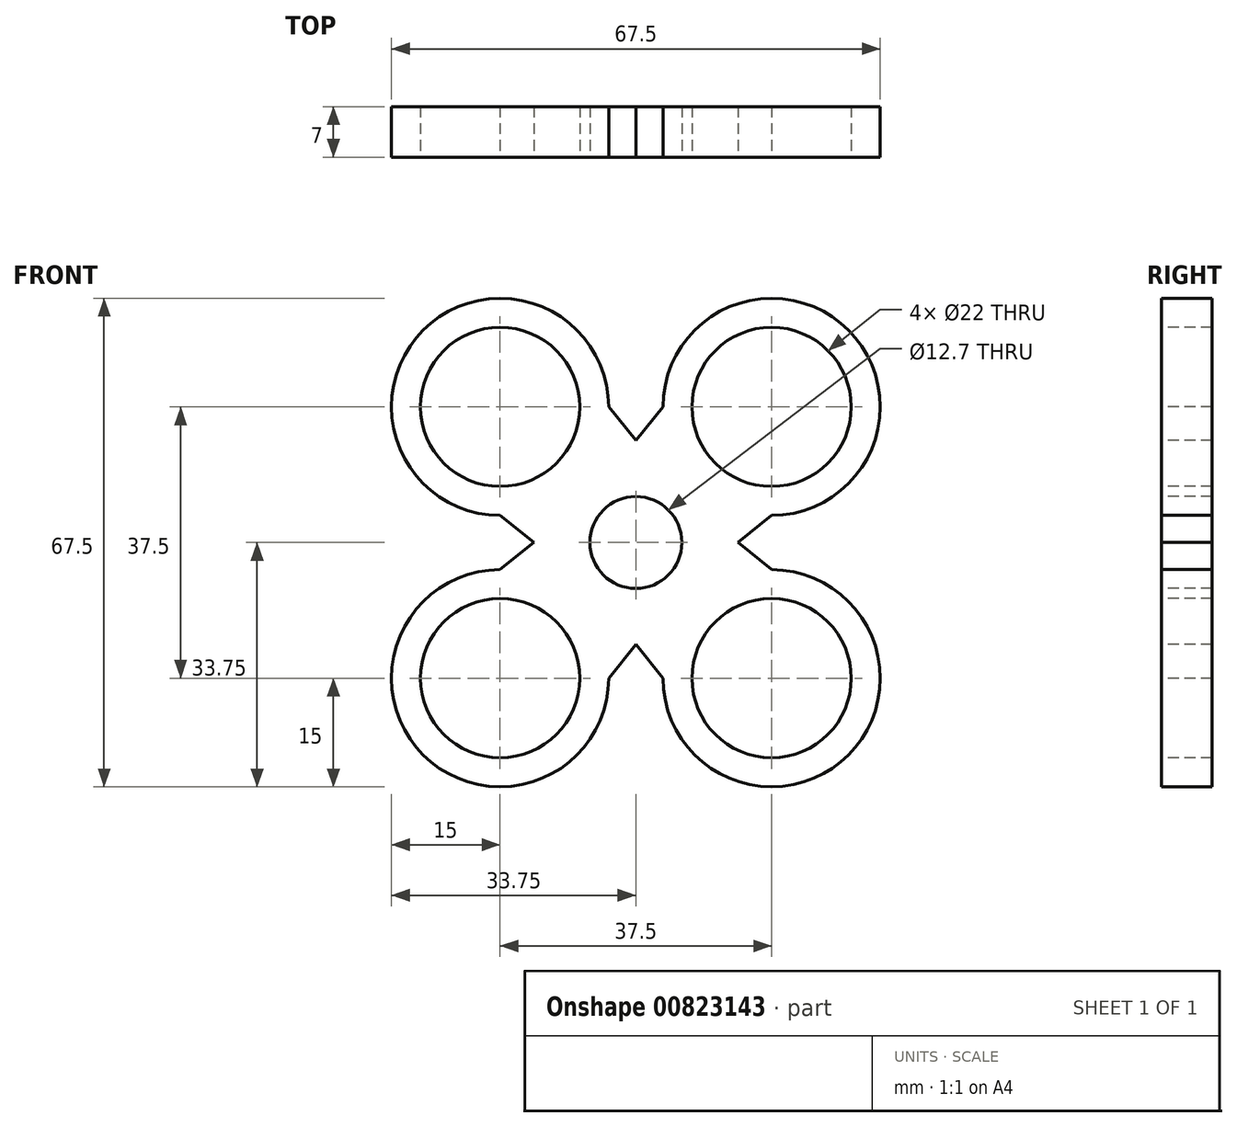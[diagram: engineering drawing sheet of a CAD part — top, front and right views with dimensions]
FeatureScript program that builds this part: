
annotation { "Feature Type Name" : "Feature", "Feature Type Description" : "" }
export const myFeature = defineFeature(function(context is Context, id is Id, definition is map)
    precondition{}
    {
        {
            var Q0;
            Q0=qCreatedBy(makeId("Front.planeOp"),FACE);
            var sketch = newSketch(context, id + "F0", { "sketchPlane" : qUnion([Q0])});
            skCircle(sketch, "E0", {"center": v(0, 0) * mm, "radius": 37.5 * mm});
            skSolve(sketch);
        }
        {
            var Q0;
            Q0=makeQuery(id+"F0.imprint","IMPRINT",FACE,{"disambiguationData":[TD([[makeQuery(id+"F0.imprint","IMPRINT",EDGE,{"derivedFrom":sQuery(id+"F0.wireOp",EDGE,"E0")}),1.0]])]});
            extrude(context, id + "F1", {"entities" : qUnion([Q0]), "depth" : 7 * mm, "offsetDistance" : 25 * mm});
        }
        {
            var Q0;
            Q0=makeQuery(id+"F1.opExtrude","CAP_FACE",FACE,{"disambiguationData":[OSD([sQuery(id+"F0.wireOp",EDGE,"E0")])],"isStart":false});
            var sketch = newSketch(context, id + "F2", { "sketchPlane" : qUnion([Q0])});
            skCircle(sketch, "E1", {"center": v(0, 0) * mm, "radius": 6.35 * mm});
            skSolve(sketch);
        }
        {
            var Q0;
            Q0=makeQuery(id+"F2.imprint","IMPRINT",FACE,{"disambiguationData":[TD([[makeQuery(id+"F2.imprint","IMPRINT",EDGE,{"derivedFrom":sQuery(id+"F2.wireOp",EDGE,"E1")}),1.0]])]});
            extrude(context, id + "F3", {"entities" : qUnion([Q0]), "operationType" : NewBodyOperationType.REMOVE, "endBound" : BoundingType.THROUGH_ALL, "oppositeDirection" : true, "depth" : 25 * mm, "offsetDistance" : 25 * mm});
        }
        {
            var Q0;
            Q0=makeQuery(id+"F1.opExtrude","CAP_FACE",FACE,{"disambiguationData":[OSD([sQuery(id+"F0.wireOp",EDGE,"E0")])],"isStart":false});
            var sketch = newSketch(context, id + "F4", { "sketchPlane" : qUnion([Q0])});
            skLineSegment(sketch, "E2", {"start": v(0, 37.5) * mm, "end": v(37.5, 0) * mm});
            skLineSegment(sketch, "E3", {"start": v(37.5, 0) * mm, "end": v(0, -37.5) * mm});
            skLineSegment(sketch, "E4", {"start": v(0, -37.5) * mm, "end": v(-37.5, 0) * mm});
            skLineSegment(sketch, "E5", {"start": v(-37.5, 0) * mm, "end": v(0, 37.5) * mm});
            skLineSegment(sketch, "E6", {"start": v(0, 37.5) * mm, "end": v(0, -37.5) * mm});
            skLineSegment(sketch, "E7", {"start": v(-37.5, 0) * mm, "end": v(37.5, 0) * mm});
            skLineSegment(sketch, "E8", {"start": v(-18.75, 18.75) * mm, "end": v(18.75, -18.75) * mm});
            skLineSegment(sketch, "E9", {"start": v(18.75, -18.75) * mm, "end": v(18.75, 18.75) * mm});
            skLineSegment(sketch, "E10", {"start": v(18.75, 18.75) * mm, "end": v(-18.75, 18.75) * mm});
            skLineSegment(sketch, "E11", {"start": v(-18.75, 18.75) * mm, "end": v(-18.75, -18.75) * mm});
            skLineSegment(sketch, "E12", {"start": v(-18.75, -18.75) * mm, "end": v(18.75, -18.75) * mm});
            skLineSegment(sketch, "E13", {"start": v(-18.75, -18.75) * mm, "end": v(18.75, 18.75) * mm});
            skCircle(sketch, "E14", {"center": v(-18.75, 18.75) * mm, "radius": 15 * mm});
            skCircle(sketch, "E15", {"center": v(-18.75, -18.75) * mm, "radius": 15 * mm});
            skCircle(sketch, "E16", {"center": v(18.75, 18.75) * mm, "radius": 15 * mm});
            skCircle(sketch, "E17", {"center": v(18.75, -18.75) * mm, "radius": 15 * mm});
            skLineSegment(sketch, "E18", {"start": v(3.75, -18.75) * mm, "end": v(0, -6.35) * mm});
            skLineSegment(sketch, "E19", {"start": v(0, -6.35) * mm, "end": v(-3.75, -18.75) * mm});
            skLineSegment(sketch, "E20", {"start": v(-3.75, -18.75) * mm, "end": v(3.75, -18.75) * mm});
            skLineSegment(sketch, "E21", {"start": v(18.75, -3.75) * mm, "end": v(6.35, 0) * mm});
            skLineSegment(sketch, "E22", {"start": v(18.75, 3.75) * mm, "end": v(6.35, 0) * mm});
            skLineSegment(sketch, "E23", {"start": v(18.75, 3.75) * mm, "end": v(18.75, -3.75) * mm});
            skLineSegment(sketch, "E24", {"start": v(-3.75, 18.75) * mm, "end": v(0, 6.35) * mm});
            skLineSegment(sketch, "E25", {"start": v(0, 6.35) * mm, "end": v(3.75, 18.75) * mm});
            skLineSegment(sketch, "E26", {"start": v(3.75, 18.75) * mm, "end": v(-3.75, 18.75) * mm});
            skLineSegment(sketch, "E27", {"start": v(-18.75, 3.75) * mm, "end": v(-6.35, 0) * mm});
            skLineSegment(sketch, "E28", {"start": v(-6.35, 0) * mm, "end": v(-18.75, -3.75) * mm});
            skLineSegment(sketch, "E29", {"start": v(-18.75, -3.75) * mm, "end": v(-18.75, 3.75) * mm});
            skLineSegment(sketch, "E30", {"start": v(18.75, -3.75) * mm, "end": v(-3.75, 18.75) * mm});
            skLineSegment(sketch, "E31", {"start": v(-18.75, 3.75) * mm, "end": v(3.75, -18.75) * mm});
            skLineSegment(sketch, "E32", {"start": v(-3.75, -18.75) * mm, "end": v(18.75, 3.75) * mm});
            skLineSegment(sketch, "E33", {"start": v(-18.75, -3.75) * mm, "end": v(3.75, 18.75) * mm});
            skLineSegment(sketch, "E34", {"start": v(-3.75, 18.75) * mm, "end": v(13, -2) * mm});
            skLineSegment(sketch, "E35", {"start": v(13, -2) * mm, "end": v(3.75, 18.75) * mm});
            skLineSegment(sketch, "E36", {"start": v(3.75, 18.75) * mm, "end": v(-13, -2) * mm});
            skLineSegment(sketch, "E37", {"start": v(-13, -2) * mm, "end": v(-3.75, 18.75) * mm});
            skLineSegment(sketch, "E38", {"start": v(-18.75, 3.75) * mm, "end": v(2, 13) * mm});
            skLineSegment(sketch, "E39", {"start": v(2, 13) * mm, "end": v(-18.75, -3.75) * mm});
            skLineSegment(sketch, "E40", {"start": v(-18.75, 3.75) * mm, "end": v(2, -13) * mm});
            skLineSegment(sketch, "E41", {"start": v(2, -13) * mm, "end": v(-18.75, -3.75) * mm});
            skLineSegment(sketch, "E42", {"start": v(-3.75, -18.75) * mm, "end": v(-13, 2) * mm});
            skLineSegment(sketch, "E43", {"start": v(-13, 2) * mm, "end": v(3.75, -18.75) * mm});
            skLineSegment(sketch, "E44", {"start": v(3.75, -18.75) * mm, "end": v(13, 2) * mm});
            skLineSegment(sketch, "E45", {"start": v(13, 2) * mm, "end": v(-3.75, -18.75) * mm});
            skLineSegment(sketch, "E46", {"start": v(18.75, 3.75) * mm, "end": v(-2, 13) * mm});
            skLineSegment(sketch, "E47", {"start": v(-2, 13) * mm, "end": v(18.75, -3.75) * mm});
            skLineSegment(sketch, "E48", {"start": v(18.75, 3.75) * mm, "end": v(-2, -13) * mm});
            skLineSegment(sketch, "E49", {"start": v(-2, -13) * mm, "end": v(18.75, -3.75) * mm});
            skSolve(sketch);
        }
        {
            var Q0;
            {var subQ0=sQuery(id+"F4.wireOp",EDGE,"E5");var subQ3=sQuery(id+"F4.wireOp",EDGE,"E14");var subQ4=makeQuery(id+"F4.imprint","INTERSECT",VERTEX,{"disambiguationData":[OD(1.0)],"derivedFrom":[subQ0,subQ3]});Q0=makeQuery(id+"F4.imprint","IMPRINT",FACE,{"disambiguationData":[TD([[makeQuery(id+"F4.imprint","IMPRINT",EDGE,{"disambiguationData":[TD([[subQ4,-1.0]])],"derivedFrom":subQ3}),-1.0]])]});}
            var Q1;
            {var subQ0=sQuery(id+"F4.wireOp",EDGE,"E2");var subQ3=sQuery(id+"F4.wireOp",EDGE,"E16");var subQ4=makeQuery(id+"F4.imprint","INTERSECT",VERTEX,{"disambiguationData":[OD(0.0)],"derivedFrom":[subQ0,subQ3]});Q1=makeQuery(id+"F4.imprint","IMPRINT",FACE,{"disambiguationData":[TD([[makeQuery(id+"F4.imprint","IMPRINT",EDGE,{"disambiguationData":[TD([[subQ4,1.0]])],"derivedFrom":subQ3}),-1.0]])]});}
            var Q2;
            {var subQ1=sQuery(id+"F4.wireOp",EDGE,"E5");var subQ3=sQuery(id+"F4.wireOp",EDGE,"E14");var subQ4=makeQuery(id+"F4.imprint","INTERSECT",VERTEX,{"disambiguationData":[OD(1.0)],"derivedFrom":[subQ1,subQ3]});Q2=makeQuery(id+"F4.imprint","IMPRINT",FACE,{"disambiguationData":[TD([[makeQuery(id+"F4.imprint","IMPRINT",EDGE,{"disambiguationData":[TD([[subQ4,-1.0]])],"derivedFrom":subQ1}),-1.0]])]});}
            var Q3;
            {var subQ1=sQuery(id+"F4.wireOp",EDGE,"E2");var subQ3=sQuery(id+"F4.wireOp",EDGE,"E16");var subQ4=makeQuery(id+"F4.imprint","INTERSECT",VERTEX,{"disambiguationData":[OD(0.0)],"derivedFrom":[subQ1,subQ3]});Q3=makeQuery(id+"F4.imprint","IMPRINT",FACE,{"disambiguationData":[TD([[makeQuery(id+"F4.imprint","IMPRINT",EDGE,{"disambiguationData":[TD([[subQ4,1.0]])],"derivedFrom":subQ1}),-1.0]])]});}
            var Q4;
            {var subQ0=sQuery(id+"F4.wireOp",EDGE,"E26");var subQ1=sQuery(id+"F4.wireOp",EDGE,"E6");var subQ2=makeQuery(id+"F4.imprint","INTERSECT",VERTEX,{"derivedFrom":[subQ1,subQ0]});Q4=makeQuery(id+"F4.imprint","IMPRINT",FACE,{"disambiguationData":[TD([[makeQuery(id+"F4.imprint","IMPRINT",EDGE,{"disambiguationData":[TD([[subQ2,-1.0]])],"derivedFrom":subQ1}),-1.0]])]});}
            var Q5;
            {var subQ0=sQuery(id+"F4.wireOp",EDGE,"E34");var subQ3=sQuery(id+"F4.wireOp",EDGE,"E33");var subQ5=makeQuery(id+"F4.imprint","INTERSECT",VERTEX,{"derivedFrom":[subQ3,subQ0]});Q5=makeQuery(id+"F4.imprint","IMPRINT",FACE,{"disambiguationData":[TD([[makeQuery(id+"F4.imprint","IMPRINT",EDGE,{"disambiguationData":[TD([[subQ5,-1.0]])],"derivedFrom":subQ3}),1.0]])]});}
            var Q6;
            {var subQ0=sQuery(id+"F4.wireOp",EDGE,"E26");var subQ1=sQuery(id+"F4.wireOp",EDGE,"E6");var subQ2=makeQuery(id+"F4.imprint","INTERSECT",VERTEX,{"derivedFrom":[subQ1,subQ0]});Q6=makeQuery(id+"F4.imprint","IMPRINT",FACE,{"disambiguationData":[TD([[makeQuery(id+"F4.imprint","IMPRINT",EDGE,{"disambiguationData":[TD([[subQ2,-1.0]])],"derivedFrom":subQ1}),1.0]])]});}
            var Q7;
            {var subQ0=sQuery(id+"F4.wireOp",EDGE,"E36");var subQ1=sQuery(id+"F4.wireOp",EDGE,"E30");var subQ2=makeQuery(id+"F4.imprint","INTERSECT",VERTEX,{"derivedFrom":[subQ1,subQ0]});Q7=makeQuery(id+"F4.imprint","IMPRINT",FACE,{"disambiguationData":[TD([[makeQuery(id+"F4.imprint","IMPRINT",EDGE,{"disambiguationData":[TD([[subQ2,-1.0]])],"derivedFrom":subQ1}),-1.0]])]});}
            var Q8;
            {var subQ0=sQuery(id+"F4.wireOp",EDGE,"E4");var subQ3=sQuery(id+"F4.wireOp",EDGE,"E15");var subQ4=makeQuery(id+"F4.imprint","INTERSECT",VERTEX,{"disambiguationData":[OD(1.0)],"derivedFrom":[subQ0,subQ3]});Q8=makeQuery(id+"F4.imprint","IMPRINT",FACE,{"disambiguationData":[TD([[makeQuery(id+"F4.imprint","IMPRINT",EDGE,{"disambiguationData":[TD([[subQ4,-1.0]])],"derivedFrom":subQ3}),-1.0]])]});}
            var Q9;
            {var subQ0=sQuery(id+"F4.wireOp",EDGE,"E5");var subQ3=sQuery(id+"F4.wireOp",EDGE,"E14");var subQ4=makeQuery(id+"F4.imprint","INTERSECT",VERTEX,{"disambiguationData":[OD(0.0)],"derivedFrom":[subQ0,subQ3]});Q9=makeQuery(id+"F4.imprint","IMPRINT",FACE,{"disambiguationData":[TD([[makeQuery(id+"F4.imprint","IMPRINT",EDGE,{"disambiguationData":[TD([[subQ4,1.0]])],"derivedFrom":subQ3}),-1.0]])]});}
            var Q10;
            {var subQ1=sQuery(id+"F4.wireOp",EDGE,"E5");var subQ3=sQuery(id+"F4.wireOp",EDGE,"E14");var subQ4=makeQuery(id+"F4.imprint","INTERSECT",VERTEX,{"disambiguationData":[OD(0.0)],"derivedFrom":[subQ1,subQ3]});Q10=makeQuery(id+"F4.imprint","IMPRINT",FACE,{"disambiguationData":[TD([[makeQuery(id+"F4.imprint","IMPRINT",EDGE,{"disambiguationData":[TD([[subQ4,1.0]])],"derivedFrom":subQ1}),-1.0]])]});}
            var Q11;
            {var subQ1=sQuery(id+"F4.wireOp",EDGE,"E4");var subQ3=sQuery(id+"F4.wireOp",EDGE,"E15");var subQ4=makeQuery(id+"F4.imprint","INTERSECT",VERTEX,{"disambiguationData":[OD(1.0)],"derivedFrom":[subQ1,subQ3]});Q11=makeQuery(id+"F4.imprint","IMPRINT",FACE,{"disambiguationData":[TD([[makeQuery(id+"F4.imprint","IMPRINT",EDGE,{"disambiguationData":[TD([[subQ4,-1.0]])],"derivedFrom":subQ1}),-1.0]])]});}
            var Q12;
            {var subQ0=sQuery(id+"F4.wireOp",EDGE,"E30");var subQ3=sQuery(id+"F4.wireOp",EDGE,"E36");var subQ5=makeQuery(id+"F4.imprint","INTERSECT",VERTEX,{"derivedFrom":[subQ0,subQ3]});Q12=makeQuery(id+"F4.imprint","IMPRINT",FACE,{"disambiguationData":[TD([[makeQuery(id+"F4.imprint","IMPRINT",EDGE,{"disambiguationData":[TD([[subQ5,-1.0]])],"derivedFrom":subQ0}),1.0]])]});}
            var Q13;
            {var subQ0=sQuery(id+"F4.wireOp",EDGE,"E33");var subQ3=sQuery(id+"F4.wireOp",EDGE,"E34");var subQ5=makeQuery(id+"F4.imprint","INTERSECT",VERTEX,{"derivedFrom":[subQ0,subQ3]});Q13=makeQuery(id+"F4.imprint","IMPRINT",FACE,{"disambiguationData":[TD([[makeQuery(id+"F4.imprint","IMPRINT",EDGE,{"disambiguationData":[TD([[subQ5,-1.0]])],"derivedFrom":subQ0}),-1.0]])]});}
            var Q14;
            {var subQ0=sQuery(id+"F4.wireOp",EDGE,"E29");var subQ1=sQuery(id+"F4.wireOp",EDGE,"E7");var subQ2=makeQuery(id+"F4.imprint","INTERSECT",VERTEX,{"derivedFrom":[subQ1,subQ0]});Q14=makeQuery(id+"F4.imprint","IMPRINT",FACE,{"disambiguationData":[TD([[makeQuery(id+"F4.imprint","IMPRINT",EDGE,{"disambiguationData":[TD([[subQ2,-1.0]])],"derivedFrom":subQ1}),1.0]])]});}
            var Q15;
            {var subQ0=sQuery(id+"F4.wireOp",EDGE,"E40");var subQ3=sQuery(id+"F4.wireOp",EDGE,"E33");var subQ5=makeQuery(id+"F4.imprint","INTERSECT",VERTEX,{"derivedFrom":[subQ3,subQ0]});Q15=makeQuery(id+"F4.imprint","IMPRINT",FACE,{"disambiguationData":[TD([[makeQuery(id+"F4.imprint","IMPRINT",EDGE,{"disambiguationData":[TD([[subQ5,1.0]])],"derivedFrom":subQ3}),1.0]])]});}
            var Q16;
            {var subQ0=sQuery(id+"F4.wireOp",EDGE,"E33");var subQ3=sQuery(id+"F4.wireOp",EDGE,"E40");var subQ5=makeQuery(id+"F4.imprint","INTERSECT",VERTEX,{"derivedFrom":[subQ0,subQ3]});Q16=makeQuery(id+"F4.imprint","IMPRINT",FACE,{"disambiguationData":[TD([[makeQuery(id+"F4.imprint","IMPRINT",EDGE,{"disambiguationData":[TD([[subQ5,1.0]])],"derivedFrom":subQ0}),-1.0]])]});}
            var Q17;
            {var subQ0=sQuery(id+"F4.wireOp",EDGE,"E31");var subQ3=sQuery(id+"F4.wireOp",EDGE,"E39");var subQ5=makeQuery(id+"F4.imprint","INTERSECT",VERTEX,{"derivedFrom":[subQ0,subQ3]});Q17=makeQuery(id+"F4.imprint","IMPRINT",FACE,{"disambiguationData":[TD([[makeQuery(id+"F4.imprint","IMPRINT",EDGE,{"disambiguationData":[TD([[subQ5,1.0]])],"derivedFrom":subQ0}),1.0]])]});}
            var Q18;
            {var subQ0=sQuery(id+"F4.wireOp",EDGE,"E39");var subQ1=sQuery(id+"F4.wireOp",EDGE,"E31");var subQ2=makeQuery(id+"F4.imprint","INTERSECT",VERTEX,{"derivedFrom":[subQ1,subQ0]});Q18=makeQuery(id+"F4.imprint","IMPRINT",FACE,{"disambiguationData":[TD([[makeQuery(id+"F4.imprint","IMPRINT",EDGE,{"disambiguationData":[TD([[subQ2,1.0]])],"derivedFrom":subQ1}),-1.0]])]});}
            var Q19;
            {var subQ0=sQuery(id+"F4.wireOp",EDGE,"E29");var subQ1=sQuery(id+"F4.wireOp",EDGE,"E7");var subQ2=makeQuery(id+"F4.imprint","INTERSECT",VERTEX,{"derivedFrom":[subQ1,subQ0]});Q19=makeQuery(id+"F4.imprint","IMPRINT",FACE,{"disambiguationData":[TD([[makeQuery(id+"F4.imprint","IMPRINT",EDGE,{"disambiguationData":[TD([[subQ2,-1.0]])],"derivedFrom":subQ1}),-1.0]])]});}
            var Q20;
            {var subQ0=sQuery(id+"F4.wireOp",EDGE,"E4");var subQ3=sQuery(id+"F4.wireOp",EDGE,"E15");var subQ4=makeQuery(id+"F4.imprint","INTERSECT",VERTEX,{"disambiguationData":[OD(0.0)],"derivedFrom":[subQ0,subQ3]});Q20=makeQuery(id+"F4.imprint","IMPRINT",FACE,{"disambiguationData":[TD([[makeQuery(id+"F4.imprint","IMPRINT",EDGE,{"disambiguationData":[TD([[subQ4,1.0]])],"derivedFrom":subQ3}),-1.0]])]});}
            var Q21;
            {var subQ0=sQuery(id+"F4.wireOp",EDGE,"E3");var subQ3=sQuery(id+"F4.wireOp",EDGE,"E17");var subQ4=makeQuery(id+"F4.imprint","INTERSECT",VERTEX,{"disambiguationData":[OD(1.0)],"derivedFrom":[subQ0,subQ3]});Q21=makeQuery(id+"F4.imprint","IMPRINT",FACE,{"disambiguationData":[TD([[makeQuery(id+"F4.imprint","IMPRINT",EDGE,{"disambiguationData":[TD([[subQ4,-1.0]])],"derivedFrom":subQ3}),-1.0]])]});}
            var Q22;
            {var subQ1=sQuery(id+"F4.wireOp",EDGE,"E3");var subQ3=sQuery(id+"F4.wireOp",EDGE,"E17");var subQ4=makeQuery(id+"F4.imprint","INTERSECT",VERTEX,{"disambiguationData":[OD(1.0)],"derivedFrom":[subQ1,subQ3]});Q22=makeQuery(id+"F4.imprint","IMPRINT",FACE,{"disambiguationData":[TD([[makeQuery(id+"F4.imprint","IMPRINT",EDGE,{"disambiguationData":[TD([[subQ4,-1.0]])],"derivedFrom":subQ1}),-1.0]])]});}
            var Q23;
            {var subQ1=sQuery(id+"F4.wireOp",EDGE,"E4");var subQ3=sQuery(id+"F4.wireOp",EDGE,"E15");var subQ4=makeQuery(id+"F4.imprint","INTERSECT",VERTEX,{"disambiguationData":[OD(0.0)],"derivedFrom":[subQ1,subQ3]});Q23=makeQuery(id+"F4.imprint","IMPRINT",FACE,{"disambiguationData":[TD([[makeQuery(id+"F4.imprint","IMPRINT",EDGE,{"disambiguationData":[TD([[subQ4,1.0]])],"derivedFrom":subQ1}),-1.0]])]});}
            var Q24;
            {var subQ0=sQuery(id+"F4.wireOp",EDGE,"E45");var subQ3=sQuery(id+"F4.wireOp",EDGE,"E31");var subQ5=makeQuery(id+"F4.imprint","INTERSECT",VERTEX,{"derivedFrom":[subQ3,subQ0]});Q24=makeQuery(id+"F4.imprint","IMPRINT",FACE,{"disambiguationData":[TD([[makeQuery(id+"F4.imprint","IMPRINT",EDGE,{"disambiguationData":[TD([[subQ5,-1.0]])],"derivedFrom":subQ3}),1.0]])]});}
            var Q25;
            {var subQ0=sQuery(id+"F4.wireOp",EDGE,"E43");var subQ3=sQuery(id+"F4.wireOp",EDGE,"E32");var subQ5=makeQuery(id+"F4.imprint","INTERSECT",VERTEX,{"derivedFrom":[subQ3,subQ0]});Q25=makeQuery(id+"F4.imprint","IMPRINT",FACE,{"disambiguationData":[TD([[makeQuery(id+"F4.imprint","IMPRINT",EDGE,{"disambiguationData":[TD([[subQ5,1.0]])],"derivedFrom":subQ3}),1.0]])]});}
            var Q26;
            {var subQ0=sQuery(id+"F4.wireOp",EDGE,"E43");var subQ3=sQuery(id+"F4.wireOp",EDGE,"E32");var subQ5=makeQuery(id+"F4.imprint","INTERSECT",VERTEX,{"derivedFrom":[subQ3,subQ0]});Q26=makeQuery(id+"F4.imprint","IMPRINT",FACE,{"disambiguationData":[TD([[makeQuery(id+"F4.imprint","IMPRINT",EDGE,{"disambiguationData":[TD([[subQ5,1.0]])],"derivedFrom":subQ3}),-1.0]])]});}
            var Q27;
            {var subQ0=sQuery(id+"F4.wireOp",EDGE,"E45");var subQ1=sQuery(id+"F4.wireOp",EDGE,"E31");var subQ2=makeQuery(id+"F4.imprint","INTERSECT",VERTEX,{"derivedFrom":[subQ1,subQ0]});Q27=makeQuery(id+"F4.imprint","IMPRINT",FACE,{"disambiguationData":[TD([[makeQuery(id+"F4.imprint","IMPRINT",EDGE,{"disambiguationData":[TD([[subQ2,-1.0]])],"derivedFrom":subQ1}),-1.0]])]});}
            var Q28;
            {var subQ0=sQuery(id+"F4.wireOp",EDGE,"E20");var subQ1=sQuery(id+"F4.wireOp",EDGE,"E6");var subQ2=makeQuery(id+"F4.imprint","INTERSECT",VERTEX,{"derivedFrom":[subQ1,subQ0]});Q28=makeQuery(id+"F4.imprint","IMPRINT",FACE,{"disambiguationData":[TD([[makeQuery(id+"F4.imprint","IMPRINT",EDGE,{"disambiguationData":[TD([[subQ2,1.0]])],"derivedFrom":subQ1}),-1.0]])]});}
            var Q29;
            {var subQ0=sQuery(id+"F4.wireOp",EDGE,"E20");var subQ1=sQuery(id+"F4.wireOp",EDGE,"E6");var subQ2=makeQuery(id+"F4.imprint","INTERSECT",VERTEX,{"derivedFrom":[subQ1,subQ0]});Q29=makeQuery(id+"F4.imprint","IMPRINT",FACE,{"disambiguationData":[TD([[makeQuery(id+"F4.imprint","IMPRINT",EDGE,{"disambiguationData":[TD([[subQ2,1.0]])],"derivedFrom":subQ1}),1.0]])]});}
            var Q30;
            {var subQ0=sQuery(id+"F4.wireOp",EDGE,"E2");var subQ3=sQuery(id+"F4.wireOp",EDGE,"E16");var subQ4=makeQuery(id+"F4.imprint","INTERSECT",VERTEX,{"disambiguationData":[OD(1.0)],"derivedFrom":[subQ0,subQ3]});Q30=makeQuery(id+"F4.imprint","IMPRINT",FACE,{"disambiguationData":[TD([[makeQuery(id+"F4.imprint","IMPRINT",EDGE,{"disambiguationData":[TD([[subQ4,-1.0]])],"derivedFrom":subQ3}),-1.0]])]});}
            var Q31;
            {var subQ1=sQuery(id+"F4.wireOp",EDGE,"E2");var subQ3=sQuery(id+"F4.wireOp",EDGE,"E16");var subQ4=makeQuery(id+"F4.imprint","INTERSECT",VERTEX,{"disambiguationData":[OD(1.0)],"derivedFrom":[subQ1,subQ3]});Q31=makeQuery(id+"F4.imprint","IMPRINT",FACE,{"disambiguationData":[TD([[makeQuery(id+"F4.imprint","IMPRINT",EDGE,{"disambiguationData":[TD([[subQ4,-1.0]])],"derivedFrom":subQ1}),-1.0]])]});}
            var Q32;
            {var subQ0=sQuery(id+"F4.wireOp",EDGE,"E3");var subQ3=sQuery(id+"F4.wireOp",EDGE,"E17");var subQ4=makeQuery(id+"F4.imprint","INTERSECT",VERTEX,{"disambiguationData":[OD(0.0)],"derivedFrom":[subQ0,subQ3]});Q32=makeQuery(id+"F4.imprint","IMPRINT",FACE,{"disambiguationData":[TD([[makeQuery(id+"F4.imprint","IMPRINT",EDGE,{"disambiguationData":[TD([[subQ4,1.0]])],"derivedFrom":subQ3}),-1.0]])]});}
            var Q33;
            {var subQ1=sQuery(id+"F4.wireOp",EDGE,"E3");var subQ3=sQuery(id+"F4.wireOp",EDGE,"E17");var subQ4=makeQuery(id+"F4.imprint","INTERSECT",VERTEX,{"disambiguationData":[OD(0.0)],"derivedFrom":[subQ1,subQ3]});Q33=makeQuery(id+"F4.imprint","IMPRINT",FACE,{"disambiguationData":[TD([[makeQuery(id+"F4.imprint","IMPRINT",EDGE,{"disambiguationData":[TD([[subQ4,1.0]])],"derivedFrom":subQ1}),-1.0]])]});}
            var Q34;
            {var subQ0=sQuery(id+"F4.wireOp",EDGE,"E48");var subQ1=sQuery(id+"F4.wireOp",EDGE,"E30");var subQ2=makeQuery(id+"F4.imprint","INTERSECT",VERTEX,{"derivedFrom":[subQ1,subQ0]});Q34=makeQuery(id+"F4.imprint","IMPRINT",FACE,{"disambiguationData":[TD([[makeQuery(id+"F4.imprint","IMPRINT",EDGE,{"disambiguationData":[TD([[subQ2,1.0]])],"derivedFrom":subQ1}),-1.0]])]});}
            var Q35;
            {var subQ0=sQuery(id+"F4.wireOp",EDGE,"E23");var subQ1=sQuery(id+"F4.wireOp",EDGE,"E7");var subQ2=makeQuery(id+"F4.imprint","INTERSECT",VERTEX,{"derivedFrom":[subQ1,subQ0]});Q35=makeQuery(id+"F4.imprint","IMPRINT",FACE,{"disambiguationData":[TD([[makeQuery(id+"F4.imprint","IMPRINT",EDGE,{"disambiguationData":[TD([[subQ2,1.0]])],"derivedFrom":subQ1}),1.0]])]});}
            var Q36;
            {var subQ0=sQuery(id+"F4.wireOp",EDGE,"E23");var subQ1=sQuery(id+"F4.wireOp",EDGE,"E7");var subQ2=makeQuery(id+"F4.imprint","INTERSECT",VERTEX,{"derivedFrom":[subQ1,subQ0]});Q36=makeQuery(id+"F4.imprint","IMPRINT",FACE,{"disambiguationData":[TD([[makeQuery(id+"F4.imprint","IMPRINT",EDGE,{"disambiguationData":[TD([[subQ2,1.0]])],"derivedFrom":subQ1}),-1.0]])]});}
            var Q37;
            {var subQ0=sQuery(id+"F4.wireOp",EDGE,"E47");var subQ3=sQuery(id+"F4.wireOp",EDGE,"E32");var subQ5=makeQuery(id+"F4.imprint","INTERSECT",VERTEX,{"derivedFrom":[subQ3,subQ0]});Q37=makeQuery(id+"F4.imprint","IMPRINT",FACE,{"disambiguationData":[TD([[makeQuery(id+"F4.imprint","IMPRINT",EDGE,{"disambiguationData":[TD([[subQ5,-1.0]])],"derivedFrom":subQ3}),-1.0]])]});}
            var Q38;
            {var subQ0=sQuery(id+"F4.wireOp",EDGE,"E47");var subQ3=sQuery(id+"F4.wireOp",EDGE,"E32");var subQ5=makeQuery(id+"F4.imprint","INTERSECT",VERTEX,{"derivedFrom":[subQ3,subQ0]});Q38=makeQuery(id+"F4.imprint","IMPRINT",FACE,{"disambiguationData":[TD([[makeQuery(id+"F4.imprint","IMPRINT",EDGE,{"disambiguationData":[TD([[subQ5,-1.0]])],"derivedFrom":subQ3}),1.0]])]});}
            var Q39;
            {var subQ0=sQuery(id+"F4.wireOp",EDGE,"E48");var subQ3=sQuery(id+"F4.wireOp",EDGE,"E30");var subQ5=makeQuery(id+"F4.imprint","INTERSECT",VERTEX,{"derivedFrom":[subQ3,subQ0]});Q39=makeQuery(id+"F4.imprint","IMPRINT",FACE,{"disambiguationData":[TD([[makeQuery(id+"F4.imprint","IMPRINT",EDGE,{"disambiguationData":[TD([[subQ5,1.0]])],"derivedFrom":subQ3}),1.0]])]});}
            extrude(context, id + "F5", {"entities" : qUnion([Q0, Q1, Q2, Q3, Q4, Q5, Q6, Q7, Q8, Q9, Q10, Q11, Q12, Q13, Q14, Q15, Q16, Q17, Q18, Q19, Q20, Q21, Q22, Q23, Q24, Q25, Q26, Q27, Q28, Q29, Q30, Q31, Q32, Q33, Q34, Q35, Q36, Q37, Q38, Q39]), "operationType" : NewBodyOperationType.REMOVE, "endBound" : BoundingType.THROUGH_ALL, "oppositeDirection" : true, "depth" : 25 * mm, "offsetDistance" : 25 * mm});
        }
        {
            var Q0;
            Q0=makeQuery(id+"F1.opExtrude","CAP_FACE",FACE,{"disambiguationData":[OSD([sQuery(id+"F0.wireOp",EDGE,"E0")])],"isStart":false});
            var sketch = newSketch(context, id + "F6", { "sketchPlane" : qUnion([Q0])});
            skCircle(sketch, "E50", {"center": v(-18.75, 18.75) * mm, "radius": 15 * mm});
            skCircle(sketch, "E51", {"center": v(-18.75, -18.75) * mm, "radius": 15 * mm});
            skCircle(sketch, "E52", {"center": v(18.75, -18.75) * mm, "radius": 15 * mm});
            skCircle(sketch, "E53", {"center": v(18.75, 18.75) * mm, "radius": 15 * mm});
            skSolve(sketch);
        }
        {
            var Q0;
            {var subQ1=sQuery(id+"F0.wireOp",EDGE,"E0");var subQ2=sQuery(id+"F4.wireOp",EDGE,"E14");var subQ3=sQuery(id+"F4.wireOp",EDGE,"E5");var subQ5=makeQuery(id+"F1.opExtrude","CAP_EDGE",EDGE,{"disambiguationData":[OSD([subQ1])],"isStart":false});var subQ6=makeQuery(id+"F4.imprint","INTERSECT",VERTEX,{"disambiguationData":[OD(1.0)],"derivedFrom":[subQ3,subQ2]});var subQ7=makeQuery(id+"F5.boolean.opBoolean","SPLIT",EDGE,{"disambiguationData":[TD([makeQuery(id+"F5.opExtrude","SWEPT_FACE",FACE,{"disambiguationData":[OSD([subQ2]),TDD([makeQuery(id+"F4.imprint","IMPRINT",EDGE,{"disambiguationData":[TD([[subQ6,1.0]])],"derivedFrom":subQ2}),makeQuery(id+"F4.imprint","IMPRINT",EDGE,{"disambiguationData":[TD([[subQ6,-1.0]])],"derivedFrom":subQ2})])]})])],"derivedFrom":subQ5});Q0=makeQuery(id+"F6.imprint","IMPRINT",FACE,{"disambiguationData":[TD([[makeQuery(id+"F6.imprint","IMPRINT",EDGE,{"derivedFrom":subQ7}),-1.0]])]});}
            var Q1;
            {var subQ1=sQuery(id+"F0.wireOp",EDGE,"E0");var subQ2=sQuery(id+"F4.wireOp",EDGE,"E15");var subQ3=sQuery(id+"F4.wireOp",EDGE,"E4");var subQ4=makeQuery(id+"F4.imprint","INTERSECT",VERTEX,{"disambiguationData":[OD(1.0)],"derivedFrom":[subQ3,subQ2]});var subQ5=makeQuery(id+"F1.opExtrude","CAP_EDGE",EDGE,{"disambiguationData":[OSD([subQ1])],"isStart":false});var subQ7=makeQuery(id+"F5.boolean.opBoolean","SPLIT",EDGE,{"disambiguationData":[TD([makeQuery(id+"F5.opExtrude","SWEPT_FACE",FACE,{"disambiguationData":[OSD([subQ2]),TDD([makeQuery(id+"F4.imprint","IMPRINT",EDGE,{"disambiguationData":[TD([[subQ4,1.0]])],"derivedFrom":subQ2}),makeQuery(id+"F4.imprint","IMPRINT",EDGE,{"disambiguationData":[TD([[subQ4,-1.0]])],"derivedFrom":subQ2})])]})])],"derivedFrom":subQ5});Q1=makeQuery(id+"F6.imprint","IMPRINT",FACE,{"disambiguationData":[TD([[makeQuery(id+"F6.imprint","IMPRINT",EDGE,{"derivedFrom":subQ7}),-1.0]])]});}
            var Q2;
            {var subQ1=sQuery(id+"F0.wireOp",EDGE,"E0");var subQ2=sQuery(id+"F4.wireOp",EDGE,"E17");var subQ3=sQuery(id+"F4.wireOp",EDGE,"E3");var subQ5=makeQuery(id+"F1.opExtrude","CAP_EDGE",EDGE,{"disambiguationData":[OSD([subQ1])],"isStart":false});var subQ6=makeQuery(id+"F4.imprint","INTERSECT",VERTEX,{"disambiguationData":[OD(0.0)],"derivedFrom":[subQ3,subQ2]});var subQ7=makeQuery(id+"F5.boolean.opBoolean","SPLIT",EDGE,{"disambiguationData":[TD([makeQuery(id+"F5.opExtrude","SWEPT_FACE",FACE,{"disambiguationData":[OSD([subQ2]),TDD([makeQuery(id+"F4.imprint","IMPRINT",EDGE,{"disambiguationData":[TD([[subQ6,1.0]])],"derivedFrom":subQ2}),makeQuery(id+"F4.imprint","IMPRINT",EDGE,{"disambiguationData":[TD([[subQ6,-1.0]])],"derivedFrom":subQ2})])]})])],"derivedFrom":subQ5});Q2=makeQuery(id+"F6.imprint","IMPRINT",FACE,{"disambiguationData":[TD([[makeQuery(id+"F6.imprint","IMPRINT",EDGE,{"derivedFrom":subQ7}),-1.0]])]});}
            var Q3;
            {var subQ1=sQuery(id+"F0.wireOp",EDGE,"E0");var subQ2=sQuery(id+"F4.wireOp",EDGE,"E16");var subQ3=sQuery(id+"F4.wireOp",EDGE,"E2");var subQ4=makeQuery(id+"F4.imprint","INTERSECT",VERTEX,{"disambiguationData":[OD(0.0)],"derivedFrom":[subQ3,subQ2]});var subQ5=makeQuery(id+"F1.opExtrude","CAP_EDGE",EDGE,{"disambiguationData":[OSD([subQ1])],"isStart":false});var subQ7=makeQuery(id+"F5.boolean.opBoolean","SPLIT",EDGE,{"disambiguationData":[TD([makeQuery(id+"F5.opExtrude","SWEPT_FACE",FACE,{"disambiguationData":[OSD([subQ2]),TDD([makeQuery(id+"F4.imprint","IMPRINT",EDGE,{"disambiguationData":[TD([[subQ4,1.0]])],"derivedFrom":subQ2}),makeQuery(id+"F4.imprint","IMPRINT",EDGE,{"disambiguationData":[TD([[subQ4,-1.0]])],"derivedFrom":subQ2})])]})])],"derivedFrom":subQ5});Q3=makeQuery(id+"F6.imprint","IMPRINT",FACE,{"disambiguationData":[TD([[makeQuery(id+"F6.imprint","IMPRINT",EDGE,{"derivedFrom":subQ7}),-1.0]])]});}
            extrude(context, id + "F7", {"entities" : qUnion([Q0, Q1, Q2, Q3]), "operationType" : NewBodyOperationType.ADD, "oppositeDirection" : true, "depth" : 7 * mm, "offsetDistance" : 25 * mm});
        }
        {
            var Q0;
            {var subQ0=sQuery(id+"F0.wireOp",EDGE,"E0");Q0=makeQuery(id+"F7.boolean.opBoolean","MERGE",FACE,{"derivedFrom":[makeQuery(id+"F1.opExtrude","CAP_FACE",FACE,{"disambiguationData":[OSD([subQ0])],"isStart":false}),makeQuery(id+"F7.opExtrude","CAP_FACE",FACE,{"disambiguationData":[OSD([subQ0,sQuery(id+"F6.wireOp",EDGE,"E50")])],"isStart":true}),makeQuery(id+"F7.opExtrude","CAP_FACE",FACE,{"disambiguationData":[OSD([subQ0,sQuery(id+"F6.wireOp",EDGE,"E51")])],"isStart":true}),makeQuery(id+"F7.opExtrude","CAP_FACE",FACE,{"disambiguationData":[OSD([subQ0,sQuery(id+"F6.wireOp",EDGE,"E52")])],"isStart":true}),makeQuery(id+"F7.opExtrude","CAP_FACE",FACE,{"disambiguationData":[OSD([subQ0,sQuery(id+"F6.wireOp",EDGE,"E53")])],"isStart":true})]});}
            var sketch = newSketch(context, id + "F8", { "sketchPlane" : qUnion([Q0])});
            skCircle(sketch, "E54", {"center": v(-18.75, 18.75) * mm, "radius": 11 * mm});
            skCircle(sketch, "E55", {"center": v(-18.75, -18.75) * mm, "radius": 11 * mm});
            skCircle(sketch, "E56", {"center": v(18.75, -18.75) * mm, "radius": 11 * mm});
            skCircle(sketch, "E57", {"center": v(18.75, 18.75) * mm, "radius": 11 * mm});
            skSolve(sketch);
        }
        {
            var Q0;
            Q0=makeQuery(id+"F8.imprint","IMPRINT",FACE,{"disambiguationData":[TD([[makeQuery(id+"F8.imprint","IMPRINT",EDGE,{"derivedFrom":sQuery(id+"F8.wireOp",EDGE,"E54")}),1.0]])]});
            var Q1;
            Q1=makeQuery(id+"F8.imprint","IMPRINT",FACE,{"disambiguationData":[TD([[makeQuery(id+"F8.imprint","IMPRINT",EDGE,{"derivedFrom":sQuery(id+"F8.wireOp",EDGE,"E57")}),1.0]])]});
            var Q2;
            Q2=makeQuery(id+"F8.imprint","IMPRINT",FACE,{"disambiguationData":[TD([[makeQuery(id+"F8.imprint","IMPRINT",EDGE,{"derivedFrom":sQuery(id+"F8.wireOp",EDGE,"E56")}),1.0]])]});
            var Q3;
            Q3=makeQuery(id+"F8.imprint","IMPRINT",FACE,{"disambiguationData":[TD([[makeQuery(id+"F8.imprint","IMPRINT",EDGE,{"derivedFrom":sQuery(id+"F8.wireOp",EDGE,"E55")}),1.0]])]});
            extrude(context, id + "F9", {"entities" : qUnion([Q0, Q1, Q2, Q3]), "operationType" : NewBodyOperationType.REMOVE, "endBound" : BoundingType.THROUGH_ALL, "oppositeDirection" : true, "depth" : 25 * mm, "offsetDistance" : 25 * mm});
        }
    });
